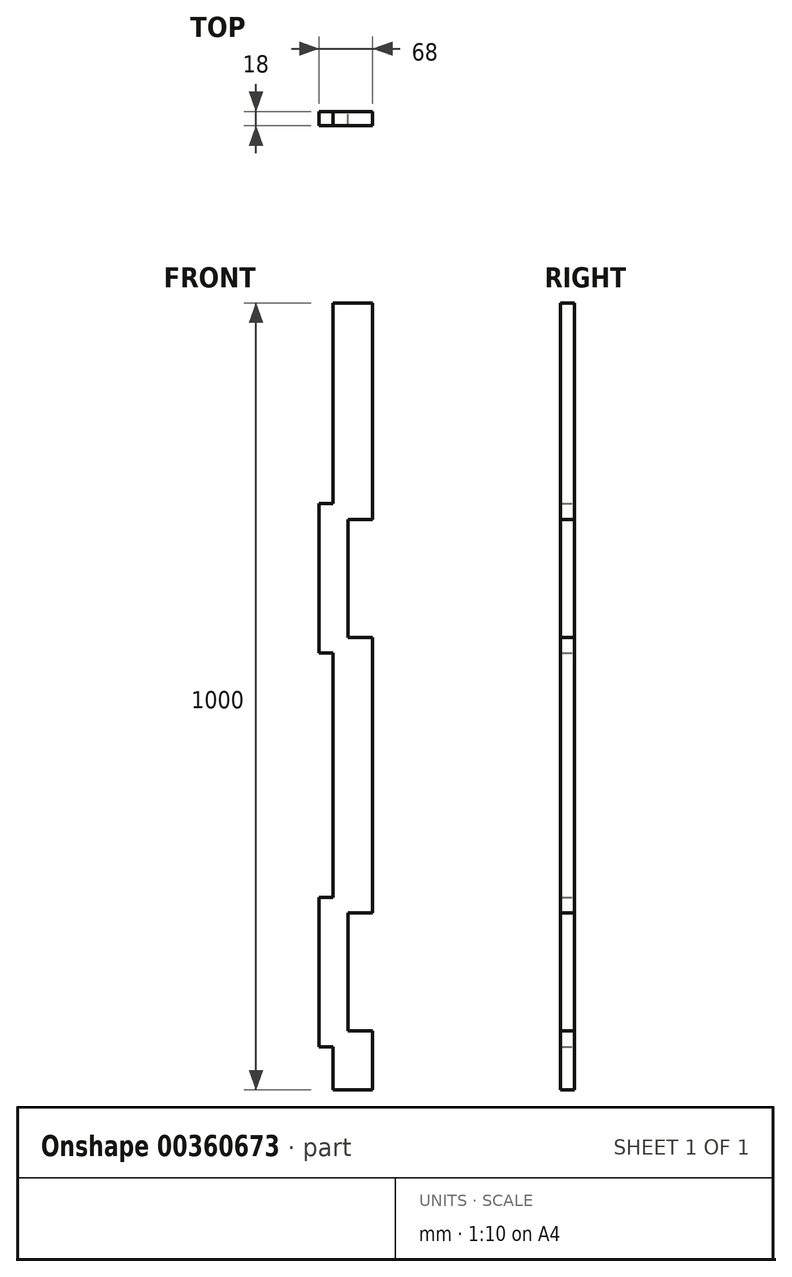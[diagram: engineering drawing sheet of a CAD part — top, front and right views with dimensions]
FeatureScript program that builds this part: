
annotation { "Feature Type Name" : "Feature", "Feature Type Description" : "" }
export const myFeature = defineFeature(function(context is Context, id is Id, definition is map)
    precondition{}
    {
        {
            var Q0;
            Q0=qCreatedBy(makeId("Front.planeOp"),FACE);
            var sketch = newSketch(context, id + "F0", { "sketchPlane" : qUnion([Q0])});
            skLineSegment(sketch, "E0.bottom", {"start": v(0, 0) * mm, "end": v(50, 0) * mm});
            skLineSegment(sketch, "E0.top", {"start": v(0, 1000) * mm, "end": v(50, 1000) * mm});
            skLineSegment(sketch, "E0.left", {"start": v(0, 0) * mm, "end": v(0, 54.64) * mm});
            skLineSegment(sketch, "E0.right", {"start": v(50, 0) * mm, "end": v(50, 75) * mm});
            skLineSegment(sketch, "E1.bottom", {"start": v(50, 725) * mm, "end": v(19, 725) * mm});
            skLineSegment(sketch, "E1.top", {"start": v(50, 575) * mm, "end": v(19, 575) * mm});
            skLineSegment(sketch, "E1.right", {"start": v(19, 725) * mm, "end": v(19, 575) * mm});
            skLineSegment(sketch, "E2.bottom", {"start": v(50, 225) * mm, "end": v(19, 225) * mm});
            skLineSegment(sketch, "E2.top", {"start": v(50, 75) * mm, "end": v(19, 75) * mm});
            skLineSegment(sketch, "E2.right", {"start": v(19, 225) * mm, "end": v(19, 75) * mm});
            skLineSegment(sketch, "E3.trimOffspring", {"start": v(50, 725) * mm, "end": v(50, 1000) * mm});
            skLineSegment(sketch, "E4.trimOffspring", {"start": v(50, 225) * mm, "end": v(50, 575) * mm});
            skLineSegment(sketch, "E5.bottom", {"start": v(-18, 745) * mm, "end": v(0, 745) * mm});
            skLineSegment(sketch, "E5.top", {"start": v(-18, 555) * mm, "end": v(0, 555) * mm});
            skLineSegment(sketch, "E5.left", {"start": v(-18, 745) * mm, "end": v(-18, 555) * mm});
            skLineSegment(sketch, "E6.trimOffspring", {"start": v(0, 745) * mm, "end": v(0, 1000) * mm});
            skLineSegment(sketch, "E7", {"start": v(0, 244.64) * mm, "end": v(-18, 244.64) * mm});
            skLineSegment(sketch, "E8", {"start": v(-18, 244.64) * mm, "end": v(-18, 54.64) * mm});
            skLineSegment(sketch, "E9", {"start": v(-18, 54.64) * mm, "end": v(0, 54.64) * mm});
            skLineSegment(sketch, "E10.trimOffspring", {"start": v(0, 244.64) * mm, "end": v(0, 555) * mm});
            skSolve(sketch);
        }
        {
            var Q0;
            Q0=makeQuery(id+"F0.imprint","IMPRINT",FACE,{"disambiguationData":[TD([[makeQuery(id+"F0.imprint","IMPRINT",EDGE,{"derivedFrom":sQuery(id+"F0.wireOp",EDGE,"E0.bottom")}),1.0]])]});
            extrude(context, id + "F1", {"entities" : qUnion([Q0]), "depth" : 18 * mm});
        }
    });
